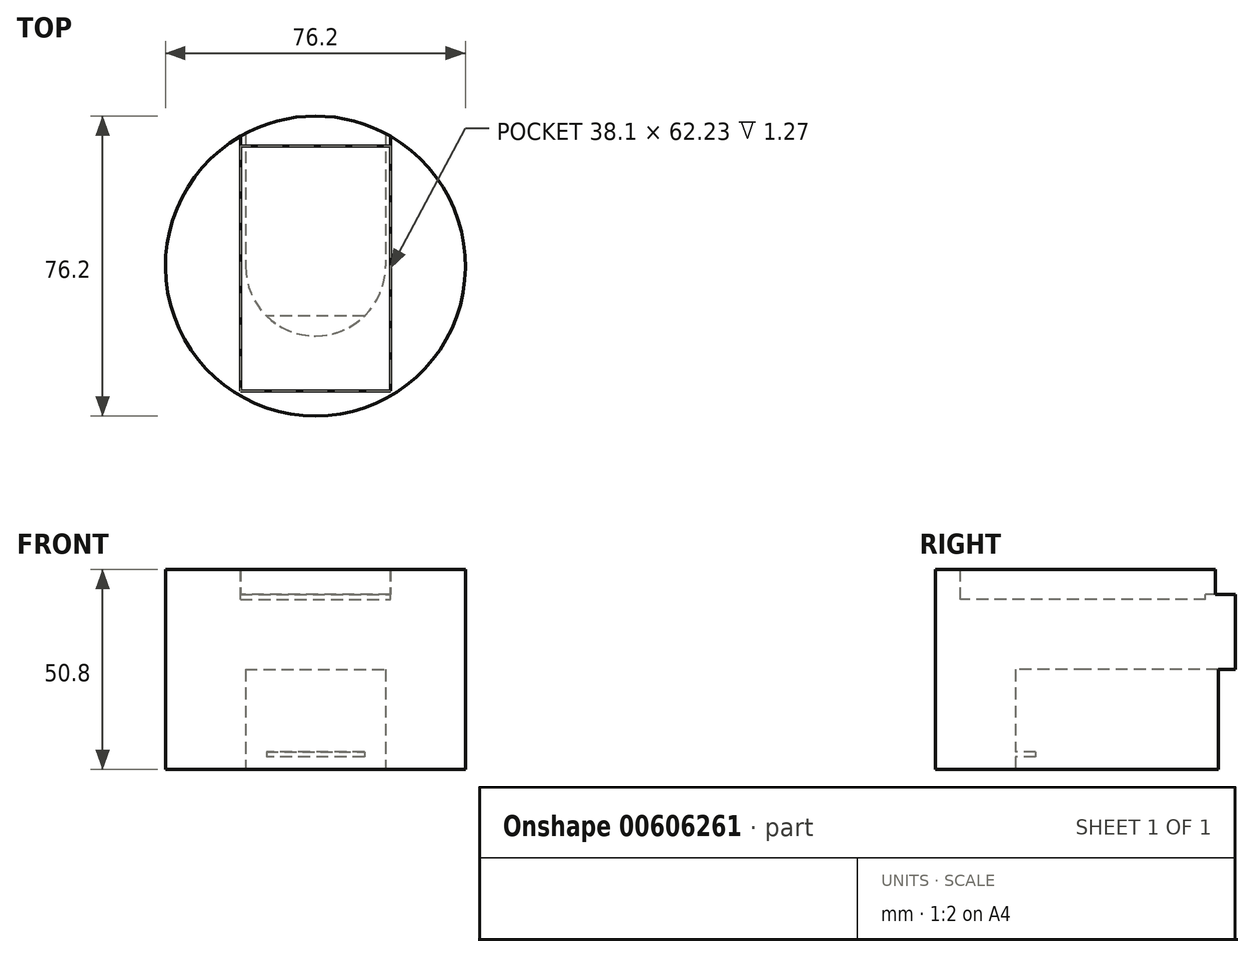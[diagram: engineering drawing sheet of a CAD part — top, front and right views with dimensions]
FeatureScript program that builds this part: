
annotation { "Feature Type Name" : "Feature", "Feature Type Description" : "" }
export const myFeature = defineFeature(function(context is Context, id is Id, definition is map)
    precondition{}
    {
        {
            var Q0;
            Q0=qCreatedBy(makeId("Top.planeOp"),FACE);
            var sketch = newSketch(context, id + "F0", { "sketchPlane" : qUnion([Q0])});
            skCircle(sketch, "E0", {"center": v(0, 0) * mm, "radius": 38.1 * mm});
            skSolve(sketch);
        }
        {
            var Q0;
            Q0 = qSketchRegion(id + "F0", true);
            extrude(context, id + "F1", {"entities" : qUnion([Q0]), "depth" : 50.8 * mm, "offsetDistance" : 25.4 * mm});
        }
        {
            var Q0;
            Q0=makeQuery(id+"F1.opExtrude","CAP_FACE",FACE,{"disambiguationData":[OSD([sQuery(id+"F0.wireOp",EDGE,"E0")])],"isStart":false});
            var sketch = newSketch(context, id + "F2", { "sketchPlane" : qUnion([Q0])});
            skLineSegment(sketch, "E1.bottom", {"start": v(-19.05, 38.1) * mm, "end": v(19.05, 38.1) * mm});
            skLineSegment(sketch, "E1.top", {"start": v(-19.05, -31.75) * mm, "end": v(19.05, -31.75) * mm});
            skLineSegment(sketch, "E1.left", {"start": v(-19.05, 38.1) * mm, "end": v(-19.05, -31.75) * mm});
            skLineSegment(sketch, "E1.right", {"start": v(19.05, 38.1) * mm, "end": v(19.05, -31.75) * mm});
            skLineSegment(sketch, "E2", {"start": v(-19.05, 30.48) * mm, "end": v(19.05, 30.48) * mm});
            skSolve(sketch);
        }
        {
            var Q0;
            Q0=makeQuery(id+"F2.imprint","IMPRINT",FACE,{"disambiguationData":[TD([[makeQuery(id+"F2.imprint","IMPRINT",EDGE,{"derivedFrom":sQuery(id+"F2.wireOp",EDGE,"E1.bottom")}),-1.0]])]});
            extrude(context, id + "F3", {"entities" : qUnion([Q0]), "operationType" : NewBodyOperationType.REMOVE, "oppositeDirection" : true, "depth" : 10.16 * mm, "offsetDistance" : 25.4 * mm});
        }
        {
            var Q0;
            {var subQ0=sQuery(id+"F2.wireOp",EDGE,"E1.right");var subQ1=sQuery(id+"F2.wireOp",EDGE,"E1.bottom");var subQ2=makeQuery(id+"F2.imprint","INTERSECT",VERTEX,{"derivedFrom":[subQ1,subQ0]});Q0=makeQuery(id+"F2.imprint","IMPRINT",FACE,{"disambiguationData":[TD([[makeQuery(id+"F2.imprint","IMPRINT",EDGE,{"disambiguationData":[TD([[subQ2,1.0]])],"derivedFrom":subQ1}),-1.0]])]});}
            var Q1;
            {var subQ0=sQuery(id+"F2.wireOp",EDGE,"E1.left");var subQ1=sQuery(id+"F2.wireOp",EDGE,"E1.bottom");var subQ2=makeQuery(id+"F2.imprint","INTERSECT",VERTEX,{"derivedFrom":[subQ1,subQ0]});Q1=makeQuery(id+"F2.imprint","IMPRINT",FACE,{"disambiguationData":[TD([[makeQuery(id+"F2.imprint","IMPRINT",EDGE,{"disambiguationData":[TD([[subQ2,-1.0]])],"derivedFrom":subQ1}),-1.0]])]});}
            var Q2;
            {var subQ4=sQuery(id+"F2.wireOp",EDGE,"E2");Q2=makeQuery(id+"F2.imprint","IMPRINT",FACE,{"disambiguationData":[TD([[makeQuery(id+"F2.imprint","IMPRINT",EDGE,{"derivedFrom":subQ4}),1.0]])]});}
            extrude(context, id + "F4", {"entities" : qUnion([Q0, Q1, Q2]), "operationType" : NewBodyOperationType.REMOVE, "oppositeDirection" : true, "depth" : 6.35 * mm, "offsetDistance" : 25.4 * mm});
        }
        {
            var Q0;
            {var subQ0=sQuery(id+"F2.wireOp",EDGE,"E1.top");Q0=makeQuery(id+"F2.imprint","IMPRINT",FACE,{"disambiguationData":[TD([[makeQuery(id+"F2.imprint","IMPRINT",EDGE,{"derivedFrom":subQ0}),1.0]])]});}
            extrude(context, id + "F5", {"entities" : qUnion([Q0]), "operationType" : NewBodyOperationType.REMOVE, "oppositeDirection" : true, "depth" : 7.62 * mm, "offsetDistance" : 25.4 * mm});
        }
        {
            var Q0;
            Q0=makeQuery(id+"F1.opExtrude","CAP_FACE",FACE,{"disambiguationData":[OSD([sQuery(id+"F0.wireOp",EDGE,"E0")])],"isStart":true});
            var sketch = newSketch(context, id + "F6", { "sketchPlane" : qUnion([Q0])});
            skCircle(sketch, "E3", {"center": v(0, 0) * mm, "radius": 17.78 * mm});
            skSolve(sketch);
        }
        {
            var Q0;
            Q0 = qSketchRegion(id + "F6", true);
            extrude(context, id + "F7", {"entities" : qUnion([Q0]), "operationType" : NewBodyOperationType.REMOVE, "oppositeDirection" : true, "depth" : 25.4 * mm, "offsetDistance" : 25.4 * mm});
        }
        {
            var Q0;
            Q0=qCreatedBy(makeId("Front.planeOp"),FACE);
            var sketch = newSketch(context, id + "F8", { "sketchPlane" : qUnion([Q0])});
            skLineSegment(sketch, "E4.bottom", {"start": v(-17.78, 0) * mm, "end": v(17.78, 0) * mm});
            skLineSegment(sketch, "E4.top", {"start": v(-17.78, 25.4) * mm, "end": v(17.78, 25.4) * mm});
            skLineSegment(sketch, "E4.left", {"start": v(-17.78, 0) * mm, "end": v(-17.78, 25.4) * mm});
            skLineSegment(sketch, "E4.right", {"start": v(17.78, 0) * mm, "end": v(17.78, 25.4) * mm});
            skSolve(sketch);
        }
        {
            var Q0;
            Q0 = qSketchRegion(id + "F8", true);
            extrude(context, id + "F9", {"entities" : qUnion([Q0]), "operationType" : NewBodyOperationType.REMOVE, "oppositeDirection" : true, "depth" : 50.8 * mm, "offsetDistance" : 25.4 * mm});
        }
        {
            var Q0;
            Q0=makeQuery(id+"F1.opExtrude","CAP_FACE",FACE,{"disambiguationData":[OSD([sQuery(id+"F0.wireOp",EDGE,"E0")])],"isStart":true});
            var sketch = newSketch(context, id + "F10", { "sketchPlane" : qUnion([Q0])});
            skLineSegment(sketch, "E5.bottom", {"start": v(-17.78, 17.78) * mm, "end": v(17.78, 17.78) * mm});
            skLineSegment(sketch, "E5.top", {"start": v(-17.78, 12.7) * mm, "end": v(17.78, 12.7) * mm});
            skLineSegment(sketch, "E5.left", {"start": v(-17.78, 17.78) * mm, "end": v(-17.78, 12.7) * mm});
            skLineSegment(sketch, "E5.right", {"start": v(17.78, 17.78) * mm, "end": v(17.78, 12.7) * mm});
            skSolve(sketch);
        }
        {
            var Q0;
            Q0 = qSketchRegion(id + "F10", true);
            extrude(context, id + "F11", {"entities" : qUnion([Q0]), "operationType" : NewBodyOperationType.ADD, "oppositeDirection" : true, "depth" : 4.44 * mm, "offsetDistance" : 25.4 * mm});
        }
        {
            var Q0;
            Q0=makeQuery(id+"F11.opExtrude","SWEPT_FACE",FACE,{"disambiguationData":[OSD([sQuery(id+"F10.wireOp",EDGE,"E5.top")])]});
            var sketch = newSketch(context, id + "F12", { "sketchPlane" : qUnion([Q0])});
            skLineSegment(sketch, "E6.bottom", {"start": v(-12.44, 0) * mm, "end": v(12.44, 0) * mm});
            skLineSegment(sketch, "E6.top", {"start": v(-12.44, 3.17) * mm, "end": v(12.44, 3.17) * mm});
            skLineSegment(sketch, "E6.left", {"start": v(-12.44, 0) * mm, "end": v(-12.44, 3.17) * mm});
            skLineSegment(sketch, "E6.right", {"start": v(12.44, 0) * mm, "end": v(12.44, 3.18) * mm});
            skSolve(sketch);
        }
        {
            var Q0;
            Q0 = qSketchRegion(id + "F12", true);
            var Q1;
            Q1=makeQuery(id+"F7.boolean.opBoolean","COPY",FACE,{"derivedFrom":makeQuery(id+"F7.opExtrude","SWEPT_FACE",FACE,{"disambiguationData":[OSD([sQuery(id+"F6.wireOp",EDGE,"E3")])]})});
            extrude(context, id + "F13", {"entities" : qUnion([Q0]), "operationType" : NewBodyOperationType.REMOVE, "endBound" : BoundingType.UP_TO_SURFACE, "oppositeDirection" : true, "depth" : 25.4 * mm, "endBoundEntityFace" : qUnion([Q1]), "offsetDistance" : 25.4 * mm});
        }
    });
